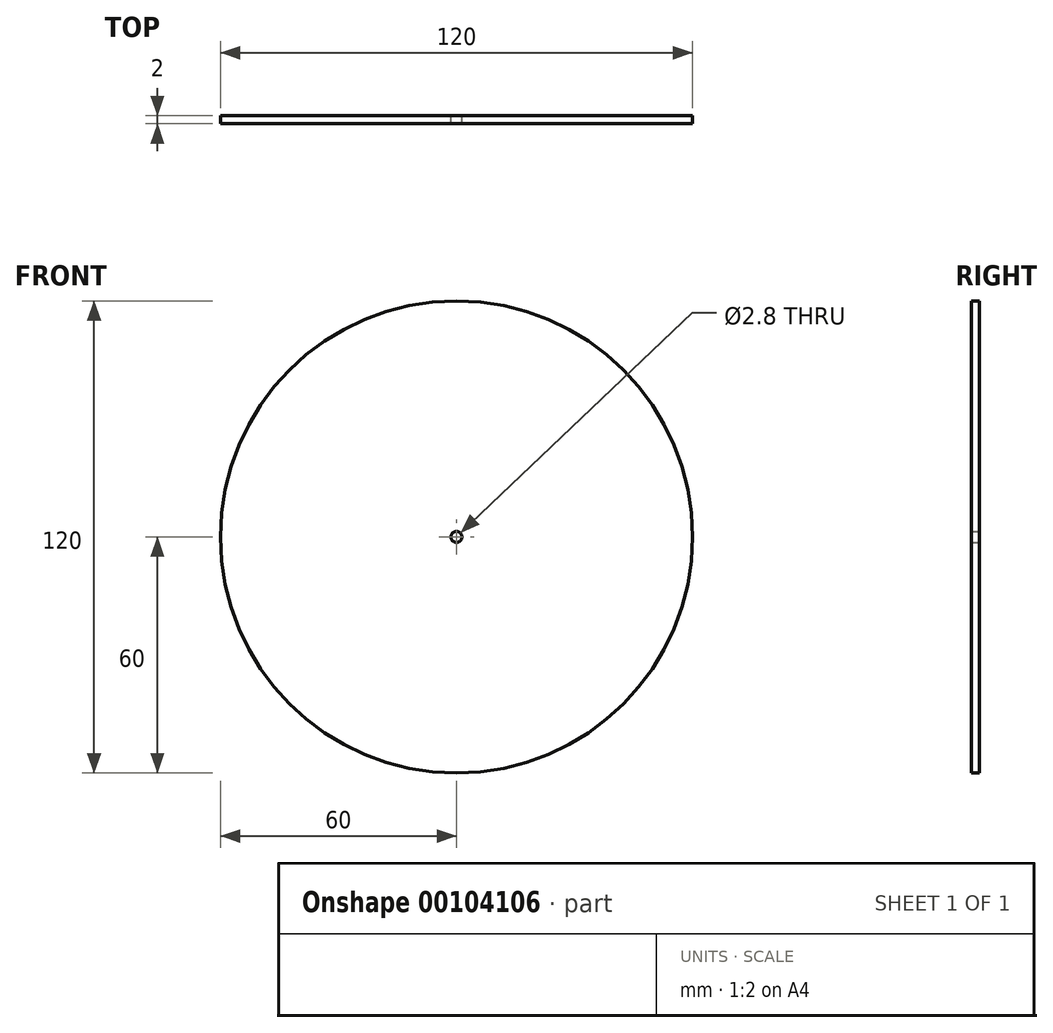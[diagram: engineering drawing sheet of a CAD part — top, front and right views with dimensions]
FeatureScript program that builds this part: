
annotation { "Feature Type Name" : "Feature", "Feature Type Description" : "" }
export const myFeature = defineFeature(function(context is Context, id is Id, definition is map)
    precondition{}
    {
        {
            var Q0;
            Q0=qCreatedBy(makeId("Front.planeOp"),FACE);
            var sketch = newSketch(context, id + "F0", { "sketchPlane" : qUnion([Q0])});
            skCircle(sketch, "E0", {"center": v(0, 0) * mm, "radius": 60 * mm});
            skCircle(sketch, "E1", {"center": v(0, 0) * mm, "radius": 1.4 * mm});
            skSolve(sketch);
        }
        {
            var Q0;
            Q0=makeQuery(id+"F0.imprint","IMPRINT",FACE,{"disambiguationData":[TD([[makeQuery(id+"F0.imprint","IMPRINT",EDGE,{"derivedFrom":sQuery(id+"F0.wireOp",EDGE,"E0")}),1.0]])]});
            extrude(context, id + "F1", {"entities" : qUnion([Q0]), "depth" : 2 * mm});
        }
    });
